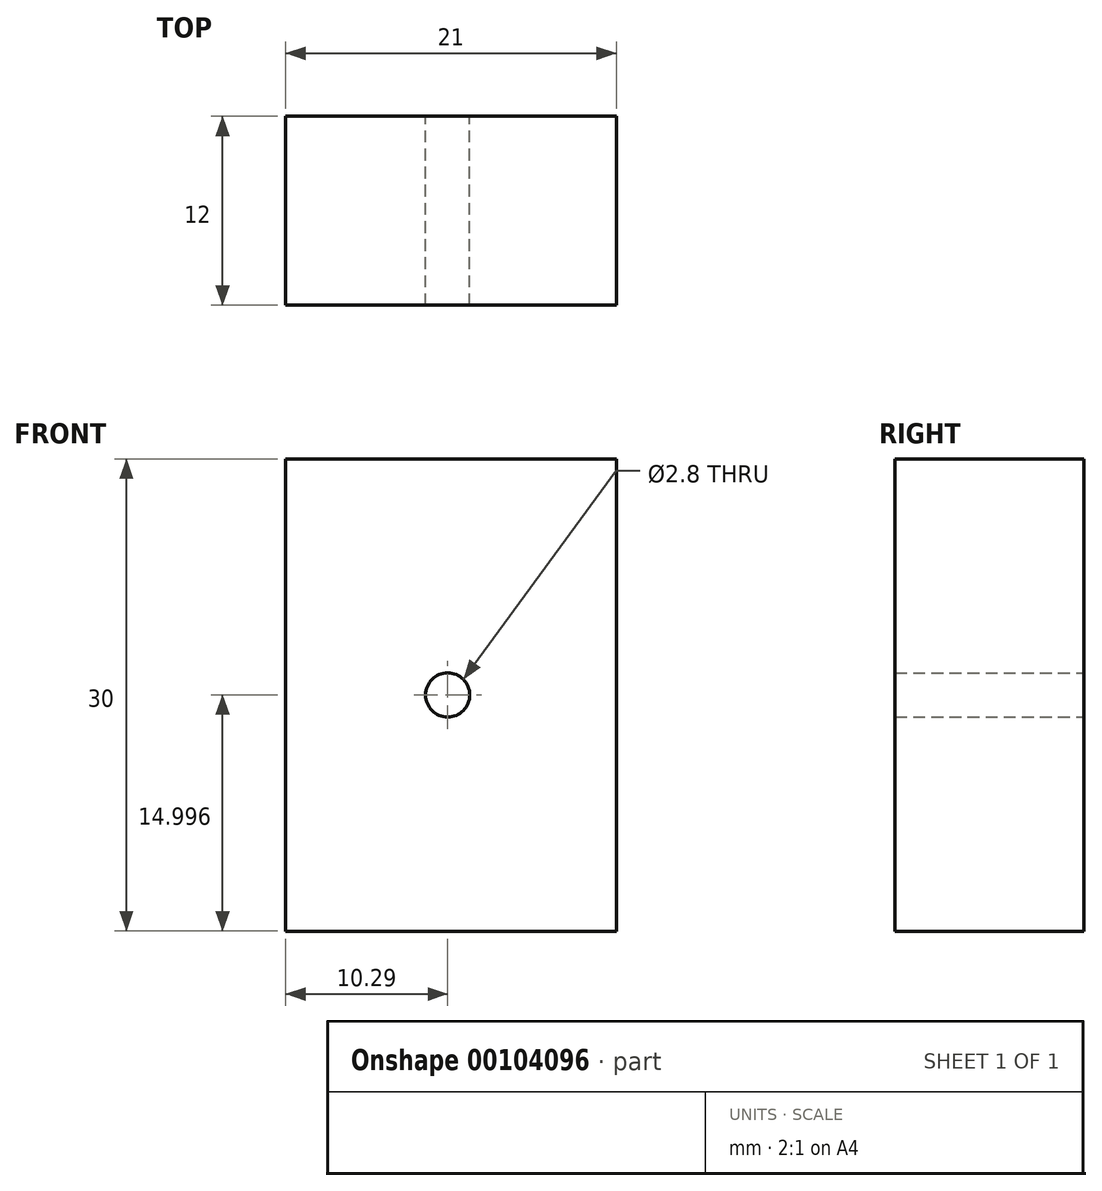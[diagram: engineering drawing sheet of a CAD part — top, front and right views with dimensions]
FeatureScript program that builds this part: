
annotation { "Feature Type Name" : "Feature", "Feature Type Description" : "" }
export const myFeature = defineFeature(function(context is Context, id is Id, definition is map)
    precondition{}
    {
        {
            var Q0;
            Q0=qCreatedBy(makeId("Front.planeOp"),FACE);
            var sketch = newSketch(context, id + "F0", { "sketchPlane" : qUnion([Q0])});
            skLineSegment(sketch, "E0.bottom", {"start": v(-10.29, 30.37) * mm, "end": v(10.71, 30.37) * mm});
            skLineSegment(sketch, "E0.top", {"start": v(-10.29, 0.37) * mm, "end": v(10.71, 0.37) * mm});
            skLineSegment(sketch, "E0.left", {"start": v(-10.29, 30.37) * mm, "end": v(-10.29, 0.37) * mm});
            skLineSegment(sketch, "E0.right", {"start": v(10.71, 30.37) * mm, "end": v(10.71, 0.37) * mm});
            skCircle(sketch, "E1", {"center": v(0, 15.37) * mm, "radius": 1.4 * mm});
            skPoint(sketch, "E1.centerSnap0", {"position": v(-10.29, 15.37) * mm});
            skSolve(sketch);
        }
        {
            var Q0;
            Q0=makeQuery(id+"F0.imprint","IMPRINT",FACE,{"disambiguationData":[TD([[makeQuery(id+"F0.imprint","IMPRINT",EDGE,{"derivedFrom":sQuery(id+"F0.wireOp",EDGE,"E0.bottom")}),-1.0]])]});
            extrude(context, id + "F1", {"entities" : qUnion([Q0]), "depth" : 12 * mm});
        }
    });
